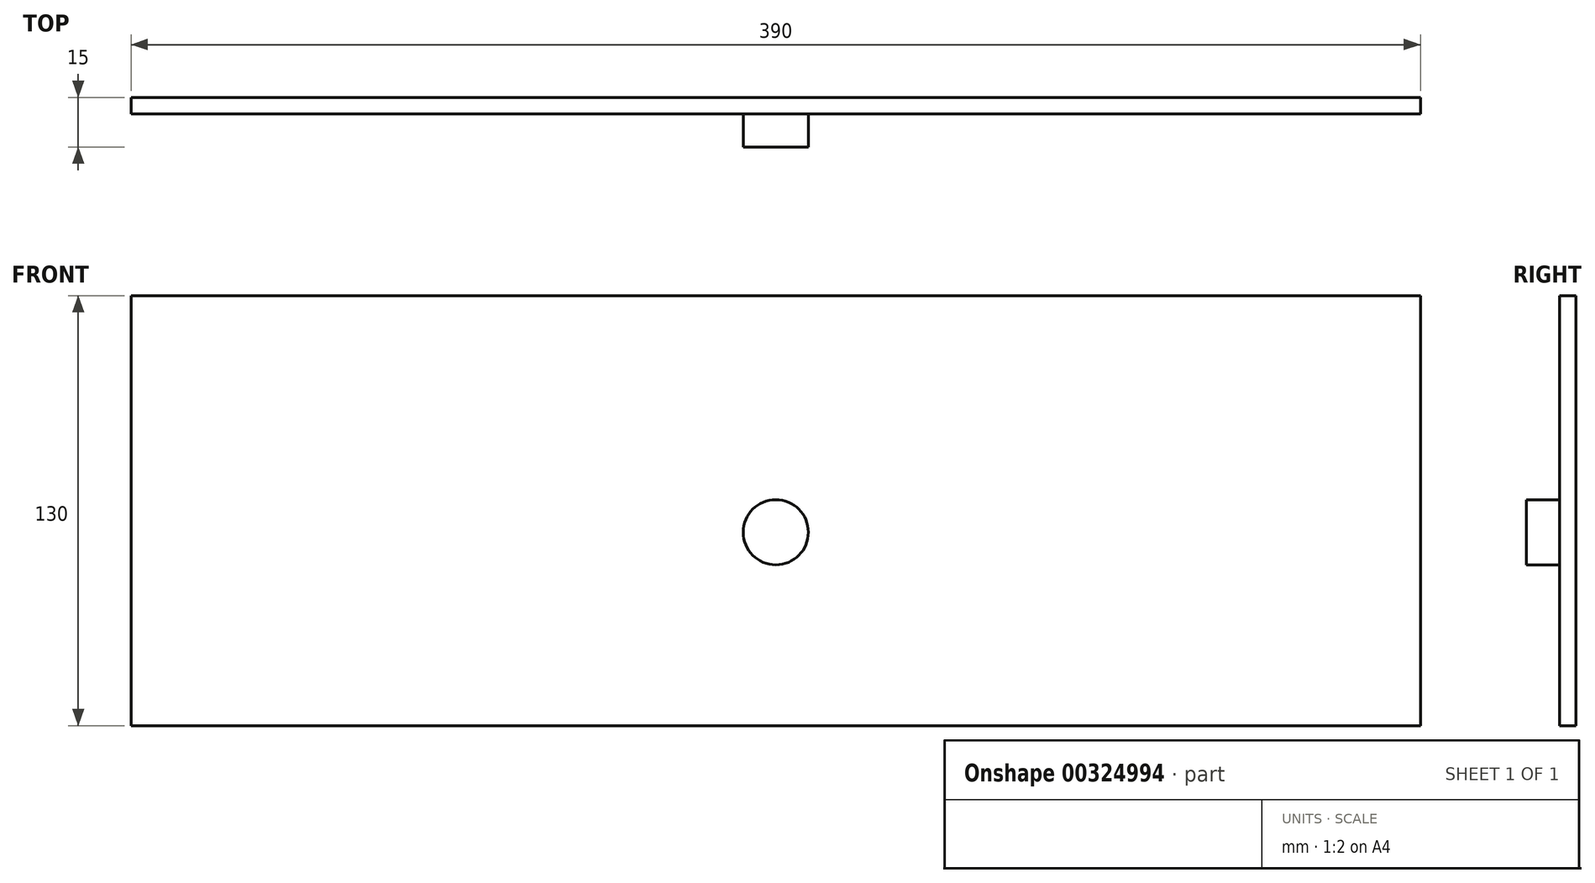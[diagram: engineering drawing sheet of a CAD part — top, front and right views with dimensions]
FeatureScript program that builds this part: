
annotation { "Feature Type Name" : "Feature", "Feature Type Description" : "" }
export const myFeature = defineFeature(function(context is Context, id is Id, definition is map)
    precondition{}
    {
        {
            var Q0;
            Q0=qCreatedBy(makeId("Front.planeOp"),FACE);
            var sketch = newSketch(context, id + "F0", { "sketchPlane" : qUnion([Q0])});
            skLineSegment(sketch, "E0", {"start": v(0, 71.53) * mm, "end": v(-195, 71.53) * mm});
            skLineSegment(sketch, "E1", {"start": v(0, 71.53) * mm, "end": v(195, 71.53) * mm});
            skLineSegment(sketch, "E2", {"start": v(-195, 71.53) * mm, "end": v(-195, -58.47) * mm});
            skLineSegment(sketch, "E3", {"start": v(-195, -58.47) * mm, "end": v(195, -58.47) * mm});
            skLineSegment(sketch, "E4", {"start": v(195, -58.47) * mm, "end": v(195, 71.53) * mm});
            skCircle(sketch, "E5", {"center": v(0, 0) * mm, "radius": 9.85 * mm});
            skSolve(sketch);
        }
        {
            var Q0;
            Q0 = qSketchRegion(id + "F0", true);
            extrude(context, id + "F1", {"entities" : qUnion([Q0]), "depth" : 5 * mm});
        }
        {
            var Q0;
            Q0=makeQuery(id+"F0.imprint","IMPRINT",FACE,{"disambiguationData":[TD([[makeQuery(id+"F0.imprint","IMPRINT",EDGE,{"derivedFrom":sQuery(id+"F0.wireOp",EDGE,"E5")}),1.0]])]});
            extrude(context, id + "F2", {"entities" : qUnion([Q0]), "operationType" : NewBodyOperationType.ADD, "depth" : 15 * mm});
        }
    });
